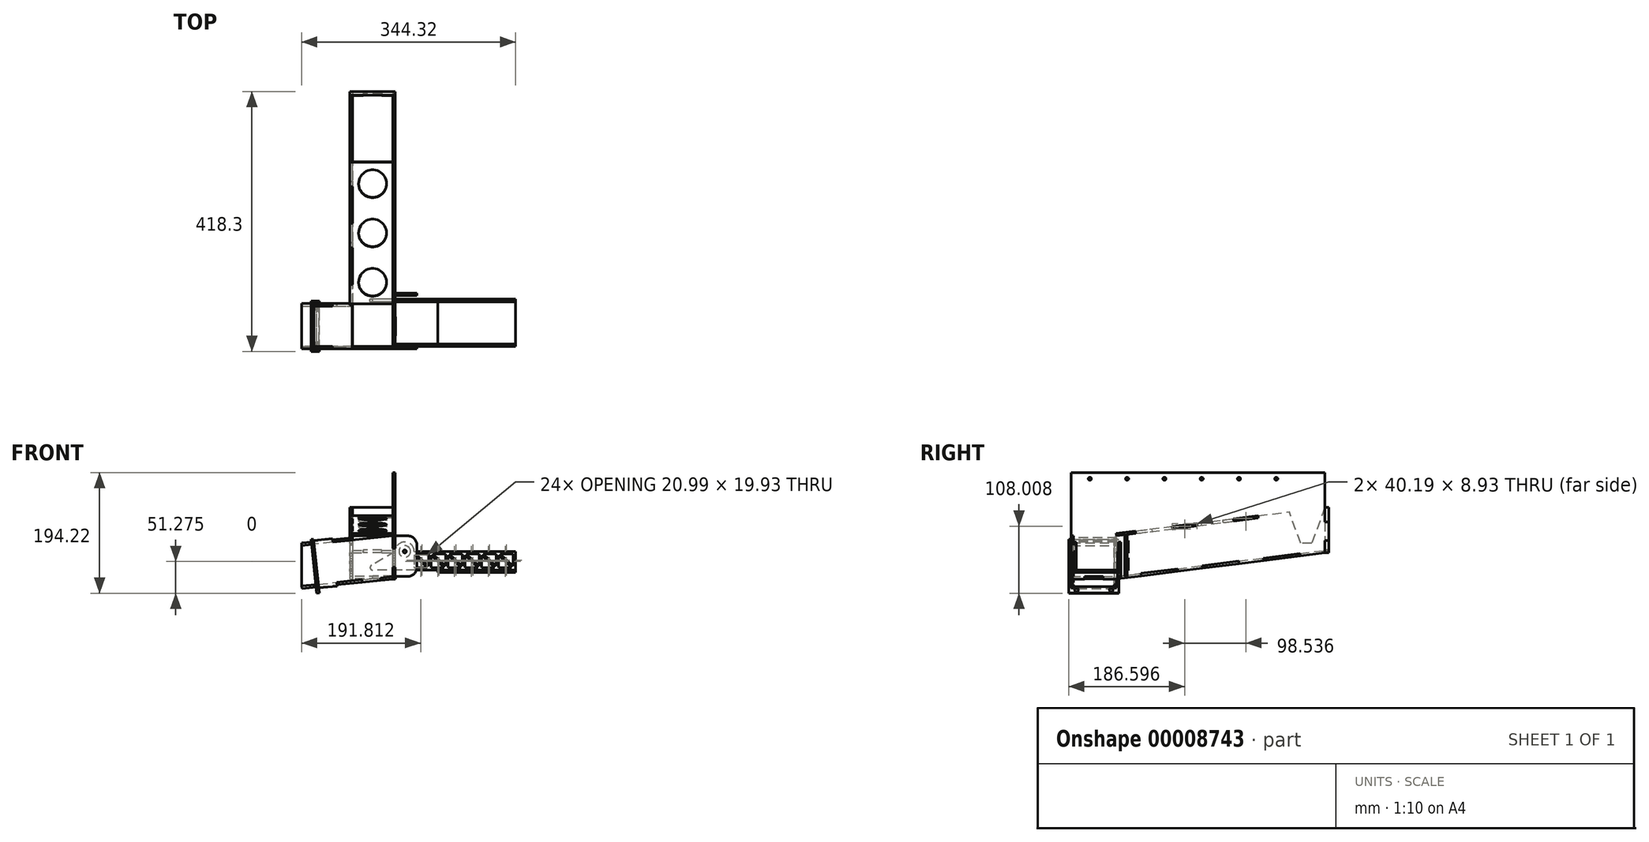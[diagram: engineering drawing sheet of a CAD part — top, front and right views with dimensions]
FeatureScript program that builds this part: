
annotation { "Feature Type Name" : "Feature", "Feature Type Description" : "" }
export const myFeature = defineFeature(function(context is Context, id is Id, definition is map)
    precondition{}
    {
        {
            var Q0;
            Q0=qCreatedBy(makeId("Front.planeOp"),FACE);
            var sketch = newSketch(context, id + "F0", { "sketchPlane" : qUnion([Q0])});
            skCircle(sketch, "E0", {"center": v(0, 0) * mm, "radius": 150 * mm, "construction": true});
            skLineSegment(sketch, "E1", {"start": v(0, 150) * mm, "end": v(0, -150) * mm, "construction": true});
            skSolve(sketch);
        }
        {
            var Q0;
            Q0=qCreatedBy(makeId("Front.planeOp"),FACE);
            var sketch = newSketch(context, id + "F1", { "sketchPlane" : qUnion([Q0])});
            skLineSegment(sketch, "E2", {"start": v(-146.4, 32.68) * mm, "end": v(-146.4, -32.68) * mm});
            skLineSegment(sketch, "E3", {"start": v(-146.4, -32.68) * mm, "end": v(-119.71, -29.87) * mm});
            skLineSegment(sketch, "E4", {"start": v(0, -17.3) * mm, "end": v(0, -2.3) * mm});
            skLineSegment(sketch, "E5", {"start": v(0, 48.07) * mm, "end": v(-96.67, 37.9) * mm});
            skLineSegment(sketch, "E6.bottom", {"start": v(0, -17.3) * mm, "end": v(-73, -17.3) * mm, "construction": true});
            skLineSegment(sketch, "E6.top", {"start": v(0, 48.07) * mm, "end": v(-73, 48.07) * mm, "construction": true});
            skLineSegment(sketch, "E6.left", {"start": v(0, -17.3) * mm, "end": v(0, 48.07) * mm, "construction": true});
            skLineSegment(sketch, "E6.right", {"start": v(-73, -17.3) * mm, "end": v(-73, 48.07) * mm, "construction": true});
            skLineSegment(sketch, "E7", {"start": v(-119.71, -29.87) * mm, "end": v(-119.09, -35.84) * mm});
            skLineSegment(sketch, "E8", {"start": v(-119.09, -35.84) * mm, "end": v(-89.25, -32.7) * mm});
            skLineSegment(sketch, "E9", {"start": v(-89.25, -32.7) * mm, "end": v(-89.88, -26.74) * mm});
            skLineSegment(sketch, "E10", {"start": v(-49.73, -22.52) * mm, "end": v(-49.3, -26.5) * mm});
            skLineSegment(sketch, "E11", {"start": v(-49.3, -26.5) * mm, "end": v(-19.47, -23.36) * mm});
            skLineSegment(sketch, "E12", {"start": v(-19.47, -23.36) * mm, "end": v(-19.9, -19.38) * mm});
            skLineSegment(sketch, "E13", {"start": v(-126.5, 34.77) * mm, "end": v(-127.13, 40.74) * mm});
            skLineSegment(sketch, "E14", {"start": v(-127.13, 40.74) * mm, "end": v(-97.3, 43.87) * mm});
            skLineSegment(sketch, "E15", {"start": v(-97.3, 43.87) * mm, "end": v(-96.67, 37.9) * mm});
            skLineSegment(sketch, "E16", {"start": v(0, 27.7) * mm, "end": v(4, 27.7) * mm});
            skLineSegment(sketch, "E17", {"start": v(4, -2.3) * mm, "end": v(0, -2.3) * mm});
            skLineSegment(sketch, "E18", {"start": v(-146.4, 32.68) * mm, "end": v(-139.6, -31.96) * mm, "construction": true});
            skLineSegment(sketch, "E19.trimOffspring", {"start": v(-89.88, -26.74) * mm, "end": v(-49.73, -22.52) * mm});
            skLineSegment(sketch, "E20.trimOffspring", {"start": v(-126.5, 34.77) * mm, "end": v(-146.4, 32.68) * mm});
            skLineSegment(sketch, "E21.trimOffspring", {"start": v(-19.9, -19.38) * mm, "end": v(0, -17.3) * mm});
            skLineSegment(sketch, "E22.trimOffspring", {"start": v(0, 27.7) * mm, "end": v(0, 48.07) * mm});
            skLineSegment(sketch, "E23.bottom", {"start": v(4, 48.07) * mm, "end": v(24, 48.07) * mm});
            skLineSegment(sketch, "E23.top", {"start": v(4, -17.3) * mm, "end": v(24, -17.3) * mm});
            skLineSegment(sketch, "E23.left", {"start": v(4, 48.07) * mm, "end": v(4, 27.7) * mm});
            skLineSegment(sketch, "E23.right", {"start": v(39, 33.07) * mm, "end": v(39, -2.3) * mm});
            skLineSegment(sketch, "E24.trimOffspring", {"start": v(4, -2.3) * mm, "end": v(4, -17.3) * mm});
            skCircle(sketch, "E25", {"center": v(19.25, 23.09) * mm, "radius": 2.5 * mm});
            skPoint(sketch, "E26.visualSharp", {"position": v(39, 48.07) * mm});
            skArc(sketch, "E26.filletArc", {"start": v(39, 33.07) * mm, "mid": v(34.6, 43.67) * mm, "end": v(24, 48.07) * mm});
            skPoint(sketch, "E27.visualSharp", {"position": v(39, -17.3) * mm});
            skArc(sketch, "E27.filletArc", {"start": v(24, -17.3) * mm, "mid": v(34.6, -12.9) * mm, "end": v(39, -2.3) * mm});
            skSolve(sketch);
        }
        {
            var Q0;
            Q0 = qSketchRegion(id + "F1", true);
            extrude(context, id + "F2", {"entities" : qUnion([Q0]), "depth" : 4 * mm});
        }
        {
            var Q0;
            Q0=makeQuery(id+"F2.opExtrude","SWEPT_FACE",FACE,{"disambiguationData":[OSD([sQuery(id+"F1.wireOp",EDGE,"E3")])]});
            var sketch = newSketch(context, id + "F3", { "sketchPlane" : qUnion([Q0])});
            skLineSegment(sketch, "E28.bottom", {"start": v(-149.01, 4) * mm, "end": v(-122.18, 4) * mm});
            skLineSegment(sketch, "E28.top", {"start": v(-149.01, -69) * mm, "end": v(-122.18, -69) * mm});
            skLineSegment(sketch, "E28.left", {"start": v(-149.01, 4) * mm, "end": v(-149.01, -69) * mm});
            skLineSegment(sketch, "E28.right", {"start": v(-1.8, 4) * mm, "end": v(-1.8, -17.5) * mm});
            skLineSegment(sketch, "E29", {"start": v(-122.18, 4) * mm, "end": v(-122.18, 0) * mm});
            skLineSegment(sketch, "E30", {"start": v(-122.18, 0) * mm, "end": v(-92.18, 0) * mm});
            skLineSegment(sketch, "E31", {"start": v(-92.18, 0) * mm, "end": v(-92.18, 4) * mm});
            skLineSegment(sketch, "E32.0.0", {"start": v(-51.8, 0) * mm, "end": v(-21.8, 0) * mm});
            skLineSegment(sketch, "E32.0.1", {"start": v(-21.8, 0) * mm, "end": v(-21.8, 4) * mm});
            skLineSegment(sketch, "E32.0.3", {"start": v(-51.8, 4) * mm, "end": v(-51.8, 0) * mm});
            skLineSegment(sketch, "E33.trimOffspring", {"start": v(-21.8, 4) * mm, "end": v(-1.8, 4) * mm});
            skLineSegment(sketch, "E34.trimOffspring", {"start": v(-92.18, 4) * mm, "end": v(-51.8, 4) * mm});
            skLineSegment(sketch, "E35", {"start": v(-1.8, -17.5) * mm, "end": v(2.2, -17.5) * mm});
            skLineSegment(sketch, "E36", {"start": v(2.2, -17.5) * mm, "end": v(2.2, -47.5) * mm});
            skLineSegment(sketch, "E37", {"start": v(2.2, -47.5) * mm, "end": v(-1.8, -47.5) * mm});
            skLineSegment(sketch, "E38.trimOffspring", {"start": v(-1.8, -47.5) * mm, "end": v(-1.8, -69) * mm});
            skLineSegment(sketch, "E39", {"start": v(-122.18, -69) * mm, "end": v(-122.18, -65) * mm});
            skLineSegment(sketch, "E40", {"start": v(-122.18, -65) * mm, "end": v(-92.18, -65) * mm});
            skLineSegment(sketch, "E41", {"start": v(-92.18, -65) * mm, "end": v(-92.18, -69) * mm});
            skLineSegment(sketch, "E42.trimOffspring", {"start": v(-92.18, -69) * mm, "end": v(-1.8, -69) * mm});
            skSolve(sketch);
        }
        {
            var Q0;
            Q0 = qSketchRegion(id + "F3", true);
            extrude(context, id + "F4", {"entities" : qUnion([Q0]), "depth" : 4 * mm});
        }
        {
            var Q0;
            Q0=makeQuery(id+"F2.opExtrude","SWEPT_FACE",FACE,{"disambiguationData":[OSD([sQuery(id+"F1.wireOp",EDGE,"E22.trimOffspring")])]});
            var sketch = newSketch(context, id + "F5", { "sketchPlane" : qUnion([Q0])});
            skLineSegment(sketch, "E43", {"start": v(404.3, 20.66) * mm, "end": v(404.3, 40.33) * mm});
            skLineSegment(sketch, "E44", {"start": v(404.3, 90) * mm, "end": v(356.07, 83.97) * mm});
            skLineSegment(sketch, "E45", {"start": v(69, 48.07) * mm, "end": v(-4, 48.07) * mm, "construction": true});
            skLineSegment(sketch, "E46", {"start": v(-4, 48.07) * mm, "end": v(-4, 27.7) * mm});
            skLineSegment(sketch, "E47", {"start": v(-4, 27.7) * mm, "end": v(0, 27.7) * mm});
            skLineSegment(sketch, "E48", {"start": v(0, 27.7) * mm, "end": v(0, -2.3) * mm});
            skLineSegment(sketch, "E49", {"start": v(0, -2.3) * mm, "end": v(-4, -2.3) * mm});
            skLineSegment(sketch, "E50", {"start": v(-4, -2.3) * mm, "end": v(-4, -21.27) * mm});
            skLineSegment(sketch, "E51", {"start": v(-4, -21.27) * mm, "end": v(17.5, -21.27) * mm});
            skLineSegment(sketch, "E52", {"start": v(17.5, -21.27) * mm, "end": v(17.5, -16.87) * mm});
            skLineSegment(sketch, "E53", {"start": v(17.5, -16.87) * mm, "end": v(47.5, -16.87) * mm});
            skLineSegment(sketch, "E54", {"start": v(47.5, -16.87) * mm, "end": v(47.5, -21.27) * mm});
            skLineSegment(sketch, "E55", {"start": v(47.5, -21.27) * mm, "end": v(69, -21.27) * mm});
            skLineSegment(sketch, "E56", {"start": v(32.5, 48.07) * mm, "end": v(32.5, -16.87) * mm, "construction": true});
            skCircle(sketch, "E57", {"center": v(32.5, 0) * mm, "radius": 150 * mm, "construction": true});
            skLineSegment(sketch, "E58", {"start": v(-117.5, 0) * mm, "end": v(-117.5, -150) * mm, "construction": true});
            skLineSegment(sketch, "E59", {"start": v(-117.5, -150) * mm, "end": v(404.3, -150) * mm, "construction": true});
            skLineSegment(sketch, "E60", {"start": v(404.3, -150) * mm, "end": v(404.3, 150) * mm, "construction": true});
            skLineSegment(sketch, "E61", {"start": v(404.3, 150) * mm, "end": v(-117.5, 150) * mm, "construction": true});
            skLineSegment(sketch, "E62", {"start": v(-117.5, 0) * mm, "end": v(-117.5, 150) * mm, "construction": true});
            skLineSegment(sketch, "E63", {"start": v(404.3, 70.33) * mm, "end": v(410.3, 70.33) * mm});
            skLineSegment(sketch, "E64", {"start": v(410.3, 70.33) * mm, "end": v(410.3, 40.33) * mm});
            skLineSegment(sketch, "E65", {"start": v(410.3, 40.33) * mm, "end": v(404.3, 40.33) * mm});
            skLineSegment(sketch, "E66.trimOffspring", {"start": v(404.3, 70.33) * mm, "end": v(404.3, 90) * mm});
            skLineSegment(sketch, "E67", {"start": v(108.7, -16.3) * mm, "end": v(108.2, -12.34) * mm});
            skLineSegment(sketch, "E68", {"start": v(108.2, -12.34) * mm, "end": v(167.04, -4.98) * mm});
            skLineSegment(sketch, "E69", {"start": v(167.04, -4.98) * mm, "end": v(167.54, -8.95) * mm});
            skLineSegment(sketch, "E70", {"start": v(207.23, -3.98) * mm, "end": v(206.73, -0.01) * mm});
            skLineSegment(sketch, "E71", {"start": v(206.73, -0.01) * mm, "end": v(265.58, 7.35) * mm});
            skLineSegment(sketch, "E72", {"start": v(265.58, 7.35) * mm, "end": v(266.07, 3.38) * mm});
            skLineSegment(sketch, "E73", {"start": v(305.76, 8.34) * mm, "end": v(305.27, 12.3) * mm});
            skLineSegment(sketch, "E74", {"start": v(305.27, 12.3) * mm, "end": v(364.11, 19.67) * mm});
            skLineSegment(sketch, "E75", {"start": v(364.11, 19.67) * mm, "end": v(364.6, 15.7) * mm});
            skLineSegment(sketch, "E76.trimOffspring", {"start": v(167.54, -8.95) * mm, "end": v(207.23, -3.98) * mm});
            skLineSegment(sketch, "E77.trimOffspring", {"start": v(364.6, 15.7) * mm, "end": v(404.3, 20.66) * mm});
            skLineSegment(sketch, "E78", {"start": v(108.7, -16.3) * mm, "end": v(76, -20.4) * mm});
            skLineSegment(sketch, "E79.trimOffspring", {"start": v(266.07, 3.38) * mm, "end": v(305.76, 8.34) * mm});
            skLineSegment(sketch, "E80", {"start": v(100.15, 51.96) * mm, "end": v(99.66, 55.93) * mm});
            skLineSegment(sketch, "E81", {"start": v(99.66, 55.93) * mm, "end": v(158.5, 63.3) * mm, "construction": true});
            skLineSegment(sketch, "E82", {"start": v(158.5, 63.3) * mm, "end": v(159, 59.32) * mm});
            skLineSegment(sketch, "E83", {"start": v(198.69, 64.29) * mm, "end": v(198.2, 68.25) * mm});
            skLineSegment(sketch, "E84", {"start": v(198.2, 68.25) * mm, "end": v(257.04, 75.61) * mm, "construction": true});
            skLineSegment(sketch, "E85", {"start": v(257.04, 75.61) * mm, "end": v(257.53, 71.64) * mm});
            skLineSegment(sketch, "E86", {"start": v(297.23, 76.6) * mm, "end": v(296.73, 80.58) * mm});
            skLineSegment(sketch, "E87", {"start": v(296.73, 80.58) * mm, "end": v(355.57, 87.94) * mm, "construction": true});
            skLineSegment(sketch, "E88", {"start": v(355.57, 87.94) * mm, "end": v(356.07, 83.97) * mm});
            skLineSegment(sketch, "E89.trimOffspring", {"start": v(100.15, 51.96) * mm, "end": v(69, 48.07) * mm});
            skLineSegment(sketch, "E90.trimOffspring", {"start": v(198.69, 64.29) * mm, "end": v(159, 59.32) * mm});
            skLineSegment(sketch, "E91.trimOffspring", {"start": v(297.23, 76.6) * mm, "end": v(257.53, 71.64) * mm});
            skLineSegment(sketch, "E92.bottom", {"start": v(71, 23.09) * mm, "end": v(76, 23.09) * mm});
            skLineSegment(sketch, "E92.top", {"start": v(71, -6.91) * mm, "end": v(76, -6.91) * mm, "construction": true});
            skLineSegment(sketch, "E92.left", {"start": v(71, 23.09) * mm, "end": v(71, -6.91) * mm});
            skLineSegment(sketch, "E92.right", {"start": v(76, 23.09) * mm, "end": v(76, -6.91) * mm});
            skLineSegment(sketch, "E93", {"start": v(76, -6.91) * mm, "end": v(76, -20.4) * mm});
            skLineSegment(sketch, "E94", {"start": v(71, -6.91) * mm, "end": v(71, -21.02) * mm});
            skLineSegment(sketch, "E95.trimOffspring", {"start": v(71, -21.02) * mm, "end": v(69, -21.27) * mm});
            skLineSegment(sketch, "E96", {"start": v(404.3, 90) * mm, "end": v(404.3, 150) * mm});
            skLineSegment(sketch, "E97", {"start": v(404.3, 150) * mm, "end": v(-4, 150) * mm});
            skLineSegment(sketch, "E98", {"start": v(-4, 48.07) * mm, "end": v(-4, 150) * mm});
            skLineSegment(sketch, "E99", {"start": v(158.5, 63.3) * mm, "end": v(198.2, 68.25) * mm});
            skLineSegment(sketch, "E100", {"start": v(257.04, 75.61) * mm, "end": v(296.73, 80.58) * mm});
            skLineSegment(sketch, "E101", {"start": v(355.57, 87.94) * mm, "end": v(404.3, 94.03) * mm});
            skLineSegment(sketch, "E102", {"start": v(69, 48.07) * mm, "end": v(68.5, 52.04) * mm});
            skLineSegment(sketch, "E103", {"start": v(68.5, 52.04) * mm, "end": v(99.66, 55.93) * mm});
            skCircle(sketch, "E104", {"center": v(26, 140) * mm, "radius": 2.5 * mm});
            skCircle(sketch, "E105", {"center": v(86, 140) * mm, "radius": 2.5 * mm});
            skCircle(sketch, "E106", {"center": v(146, 140) * mm, "radius": 2.5 * mm});
            skCircle(sketch, "E107", {"center": v(206, 140) * mm, "radius": 2.5 * mm});
            skCircle(sketch, "E108", {"center": v(266, 140) * mm, "radius": 2.5 * mm});
            skCircle(sketch, "E109", {"center": v(326, 140) * mm, "radius": 2.5 * mm});
            skCircle(sketch, "E110", {"center": v(374.3, 120) * mm, "radius": 30 * mm, "construction": true});
            skLineSegment(sketch, "E111.bottom", {"start": v(82, 40.6) * mm, "end": v(88, 40.6) * mm});
            skLineSegment(sketch, "E111.top", {"start": v(82, 20.6) * mm, "end": v(88, 20.6) * mm});
            skLineSegment(sketch, "E111.left", {"start": v(82, 40.6) * mm, "end": v(82, 20.6) * mm});
            skLineSegment(sketch, "E111.right", {"start": v(88, 40.6) * mm, "end": v(88, 20.6) * mm});
            skLineSegment(sketch, "E112.bottom", {"start": v(82, 12.6) * mm, "end": v(88, 12.6) * mm});
            skLineSegment(sketch, "E112.top", {"start": v(82, -7.4) * mm, "end": v(88, -7.4) * mm});
            skLineSegment(sketch, "E112.left", {"start": v(82, 12.6) * mm, "end": v(82, -7.4) * mm});
            skLineSegment(sketch, "E112.right", {"start": v(88, 12.6) * mm, "end": v(88, -7.4) * mm});
            skSolve(sketch);
        }
        {
            var Q0;
            Q0 = qSketchRegion(id + "F5", true);
            extrude(context, id + "F6", {"entities" : qUnion([Q0]), "depth" : 4 * mm});
        }
        {
            var Q0;
            Q0=makeQuery(id+"F6.opExtrude","SWEPT_FACE",FACE,{"disambiguationData":[OSD([sQuery(id+"F5.wireOp",EDGE,"E71")])]});
            var sketch = newSketch(context, id + "F7", { "sketchPlane" : qUnion([Q0])});
            skLineSegment(sketch, "E113", {"start": v(-65, -66.32) * mm, "end": v(-65, -105.83) * mm});
            skLineSegment(sketch, "E114", {"start": v(-65, -403.74) * mm, "end": v(-47.5, -403.74) * mm});
            skLineSegment(sketch, "E115", {"start": v(4, -363.74) * mm, "end": v(4, -304.44) * mm});
            skLineSegment(sketch, "E116.0.0", {"start": v(0, -363.74) * mm, "end": v(0, -403.74) * mm});
            skLineSegment(sketch, "E116.0.3", {"start": v(4, -363.74) * mm, "end": v(0, -363.74) * mm});
            skPoint(sketch, "E116.0.1.end.orphan", {"position": v(4, -403.74) * mm});
            skLineSegment(sketch, "E117.0.0", {"start": v(0, -264.44) * mm, "end": v(0, -304.44) * mm});
            skLineSegment(sketch, "E117.0.1", {"start": v(0, -304.44) * mm, "end": v(4, -304.44) * mm});
            skLineSegment(sketch, "E117.0.3", {"start": v(4, -264.44) * mm, "end": v(0, -264.44) * mm});
            skLineSegment(sketch, "E118.trimOffspring", {"start": v(4, -264.44) * mm, "end": v(4, -205.13) * mm});
            skLineSegment(sketch, "E119.0.0", {"start": v(0, -165.13) * mm, "end": v(0, -205.13) * mm});
            skLineSegment(sketch, "E119.0.1", {"start": v(0, -205.13) * mm, "end": v(4, -205.13) * mm});
            skLineSegment(sketch, "E119.0.3", {"start": v(4, -165.13) * mm, "end": v(0, -165.13) * mm});
            skLineSegment(sketch, "E120.trimOffspring", {"start": v(4, -165.13) * mm, "end": v(4, -105.83) * mm});
            skLineSegment(sketch, "E121.0.0", {"start": v(0, -66.32) * mm, "end": v(0, -67.38) * mm});
            skLineSegment(sketch, "E121.0.1", {"start": v(0, -105.83) * mm, "end": v(4, -105.83) * mm});
            skLineSegment(sketch, "E122", {"start": v(0, -66.32) * mm, "end": v(-65, -66.32) * mm});
            skLineSegment(sketch, "E123", {"start": v(-32.5, -403.74) * mm, "end": v(-32.5, -66.32) * mm, "construction": true});
            skLineSegment(sketch, "E124.0.MirrorCS", {"start": v(-65, -105.83) * mm, "end": v(-69, -105.83) * mm});
            skLineSegment(sketch, "E125.0.MirrorCS", {"start": v(-69, -165.13) * mm, "end": v(-69, -105.83) * mm});
            skLineSegment(sketch, "E126.0.MirrorCS", {"start": v(-69, -165.13) * mm, "end": v(-65, -165.13) * mm});
            skLineSegment(sketch, "E127.0.MirrorCS", {"start": v(-65, -205.13) * mm, "end": v(-69, -205.13) * mm});
            skLineSegment(sketch, "E128.0.MirrorCS", {"start": v(-69, -264.44) * mm, "end": v(-69, -205.13) * mm});
            skLineSegment(sketch, "E129.0.MirrorCS", {"start": v(-69, -264.44) * mm, "end": v(-65, -264.44) * mm});
            skLineSegment(sketch, "E130.0.MirrorCS", {"start": v(-65, -304.44) * mm, "end": v(-69, -304.44) * mm});
            skLineSegment(sketch, "E131.0.MirrorCS", {"start": v(-69, -363.74) * mm, "end": v(-69, -304.44) * mm});
            skLineSegment(sketch, "E132.0.MirrorCS", {"start": v(-69, -363.74) * mm, "end": v(-65, -363.74) * mm});
            skLineSegment(sketch, "E133.trimOffspring", {"start": v(-65, -165.13) * mm, "end": v(-65, -205.13) * mm});
            skLineSegment(sketch, "E134.trimOffspring", {"start": v(-65, -264.44) * mm, "end": v(-65, -304.44) * mm});
            skLineSegment(sketch, "E135.trimOffspring", {"start": v(-65, -363.74) * mm, "end": v(-65, -403.74) * mm});
            skLineSegment(sketch, "E136", {"start": v(-17.5, -403.74) * mm, "end": v(-17.5, -407.74) * mm});
            skLineSegment(sketch, "E137", {"start": v(-17.5, -407.74) * mm, "end": v(-47.5, -407.74) * mm});
            skLineSegment(sketch, "E138", {"start": v(-47.5, -407.74) * mm, "end": v(-47.5, -403.74) * mm});
            skLineSegment(sketch, "E139.trimOffspring", {"start": v(-17.5, -403.74) * mm, "end": v(0, -403.74) * mm});
            skLineSegment(sketch, "E140.bottom", {"start": v(0, -67.38) * mm, "end": v(-32.5, -67.38) * mm});
            skLineSegment(sketch, "E140.top", {"start": v(0, -73.38) * mm, "end": v(-32.5, -73.38) * mm});
            skLineSegment(sketch, "E140.right", {"start": v(-32.5, -67.38) * mm, "end": v(-32.5, -73.38) * mm});
            skLineSegment(sketch, "E141.trimOffspring", {"start": v(0, -73.38) * mm, "end": v(0, -105.83) * mm});
            skSolve(sketch);
        }
        {
            var Q0;
            Q0 = qSketchRegion(id + "F7", true);
            extrude(context, id + "F8", {"entities" : qUnion([Q0]), "depth" : 4 * mm});
        }
        {
            var Q0;
            Q0=makeQuery(id+"F8.opExtrude","SWEPT_FACE",FACE,{"disambiguationData":[OSD([sQuery(id+"F7.wireOp",EDGE,"E135.trimOffspring")])]});
            var sketch = newSketch(context, id + "F9", { "sketchPlane" : qUnion([Q0])});
            skLineSegment(sketch, "E142.0.0", {"start": v(-404.3, 20.66) * mm, "end": v(-364.6, 15.7) * mm});
            skLineSegment(sketch, "E142.0.1", {"start": v(-364.6, 15.7) * mm, "end": v(-364.11, 19.67) * mm});
            skLineSegment(sketch, "E142.0.2", {"start": v(-364.11, 19.67) * mm, "end": v(-305.27, 12.3) * mm});
            skLineSegment(sketch, "E142.0.3", {"start": v(-305.27, 12.3) * mm, "end": v(-305.76, 8.34) * mm});
            skLineSegment(sketch, "E142.0.4", {"start": v(-305.76, 8.34) * mm, "end": v(-266.07, 3.38) * mm});
            skLineSegment(sketch, "E142.0.5", {"start": v(-266.07, 3.38) * mm, "end": v(-265.58, 7.35) * mm});
            skLineSegment(sketch, "E142.0.6", {"start": v(-265.58, 7.35) * mm, "end": v(-206.73, -0.01) * mm});
            skLineSegment(sketch, "E142.0.7", {"start": v(-206.73, -0.01) * mm, "end": v(-207.23, -3.98) * mm});
            skLineSegment(sketch, "E142.0.8", {"start": v(-207.23, -3.98) * mm, "end": v(-167.54, -8.95) * mm});
            skLineSegment(sketch, "E142.0.9", {"start": v(-167.54, -8.95) * mm, "end": v(-167.04, -4.98) * mm});
            skLineSegment(sketch, "E142.0.10", {"start": v(-167.04, -4.98) * mm, "end": v(-108.2, -12.34) * mm});
            skLineSegment(sketch, "E142.0.11", {"start": v(-108.2, -12.34) * mm, "end": v(-108.7, -16.3) * mm});
            skLineSegment(sketch, "E142.0.12", {"start": v(-108.7, -16.3) * mm, "end": v(-69, -21.27) * mm});
            skLineSegment(sketch, "E142.0.24", {"start": v(-69, 48.07) * mm, "end": v(-100.15, 51.96) * mm});
            skLineSegment(sketch, "E142.0.25", {"start": v(-99.66, 55.93) * mm, "end": v(-100.15, 51.96) * mm});
            skLineSegment(sketch, "E142.0.26", {"start": v(-99.66, 55.93) * mm, "end": v(-158.5, 63.3) * mm});
            skLineSegment(sketch, "E142.0.27", {"start": v(-158.5, 63.3) * mm, "end": v(-159, 59.32) * mm});
            skLineSegment(sketch, "E142.0.28", {"start": v(-159, 59.32) * mm, "end": v(-198.69, 64.29) * mm});
            skLineSegment(sketch, "E142.0.29", {"start": v(-198.2, 68.25) * mm, "end": v(-198.69, 64.29) * mm});
            skLineSegment(sketch, "E142.0.30", {"start": v(-198.2, 68.25) * mm, "end": v(-257.04, 75.61) * mm});
            skLineSegment(sketch, "E142.0.31", {"start": v(-257.04, 75.61) * mm, "end": v(-257.53, 71.64) * mm});
            skLineSegment(sketch, "E142.0.32", {"start": v(-257.53, 71.64) * mm, "end": v(-297.23, 76.6) * mm});
            skLineSegment(sketch, "E142.0.33", {"start": v(-296.73, 80.58) * mm, "end": v(-297.23, 76.6) * mm});
            skLineSegment(sketch, "E142.0.34", {"start": v(-296.73, 80.58) * mm, "end": v(-346.91, 86.85) * mm});
            skLineSegment(sketch, "E142.0.37", {"start": v(-404.3, 94.03) * mm, "end": v(-404.3, 70.33) * mm});
            skLineSegment(sketch, "E142.0.38", {"start": v(-404.3, 70.33) * mm, "end": v(-410.3, 70.33) * mm});
            skLineSegment(sketch, "E142.0.39", {"start": v(-410.3, 70.33) * mm, "end": v(-410.3, 40.33) * mm});
            skLineSegment(sketch, "E142.0.40", {"start": v(-410.3, 40.33) * mm, "end": v(-404.3, 40.33) * mm});
            skLineSegment(sketch, "E142.0.41", {"start": v(-404.3, 40.33) * mm, "end": v(-404.3, 20.66) * mm});
            skLineSegment(sketch, "E143", {"start": v(-69, 45.23) * mm, "end": v(-69, 32.95) * mm});
            skLineSegment(sketch, "E144", {"start": v(-69, 32.95) * mm, "end": v(-65, 32.95) * mm});
            skLineSegment(sketch, "E145", {"start": v(-65, 32.95) * mm, "end": v(-65, 20.95) * mm});
            skLineSegment(sketch, "E146", {"start": v(-65, 20.95) * mm, "end": v(-69, 20.95) * mm});
            skLineSegment(sketch, "E147", {"start": v(-69, 5.84) * mm, "end": v(-65, 5.84) * mm});
            skLineSegment(sketch, "E148", {"start": v(-65, 5.84) * mm, "end": v(-65, -6.16) * mm});
            skLineSegment(sketch, "E149", {"start": v(-65, -6.16) * mm, "end": v(-69, -6.16) * mm});
            skLineSegment(sketch, "E150.trimOffspring", {"start": v(-69, 20.95) * mm, "end": v(-69, 5.84) * mm});
            skLineSegment(sketch, "E151.trimOffspring", {"start": v(-69, -6.16) * mm, "end": v(-69, -21.27) * mm});
            skCircle(sketch, "E152", {"center": v(-374.3, 51.18) * mm, "radius": 30 * mm, "construction": true});
            skLineSegment(sketch, "E153", {"start": v(-404.3, 94.03) * mm, "end": v(-383.24, 36.18) * mm});
            skLineSegment(sketch, "E154", {"start": v(-383.24, 36.18) * mm, "end": v(-365.36, 36.18) * mm});
            skLineSegment(sketch, "E155", {"start": v(-365.36, 36.18) * mm, "end": v(-346.91, 86.85) * mm});
            skLineSegment(sketch, "E156", {"start": v(-374.3, 36.18) * mm, "end": v(-374.3, 81.18) * mm, "construction": true});
            skPoint(sketch, "E142.0.35.end.orphan", {"position": v(-356.78, 84.6) * mm});
            skPoint(sketch, "E142.0.35.start.orphan", {"position": v(-355.27, 87.9) * mm});
            skLineSegment(sketch, "E157", {"start": v(-69, 48.07) * mm, "end": v(-67, 48.07) * mm});
            skLineSegment(sketch, "E158", {"start": v(-67, 48.07) * mm, "end": v(-67, 45.23) * mm});
            skLineSegment(sketch, "E159", {"start": v(-67, 45.23) * mm, "end": v(-69, 45.23) * mm});
            skLineSegment(sketch, "E160", {"start": v(-69, 32.95) * mm, "end": v(-69, 48.07) * mm, "construction": true});
            skSolve(sketch);
        }
        {
            var Q0;
            Q0 = qSketchRegion(id + "F9", true);
            extrude(context, id + "F10", {"entities" : qUnion([Q0]), "depth" : 4 * mm});
        }
        {
            var Q0;
            Q0=makeQuery(id+"F4.opExtrude","SWEPT_FACE",FACE,{"disambiguationData":[OSD([sQuery(id+"F3.wireOp",EDGE,"E28.top")])]});
            var sketch = newSketch(context, id + "F11", { "sketchPlane" : qUnion([Q0])});
            skLineSegment(sketch, "E161", {"start": v(146.4, -32.68) * mm, "end": v(146.4, 32.68) * mm});
            skLineSegment(sketch, "E162", {"start": v(146.4, 32.68) * mm, "end": v(126.5, 34.77) * mm});
            skLineSegment(sketch, "E163", {"start": v(126.5, 34.77) * mm, "end": v(127.13, 40.74) * mm});
            skLineSegment(sketch, "E164", {"start": v(127.13, 40.74) * mm, "end": v(97.3, 43.87) * mm});
            skLineSegment(sketch, "E165", {"start": v(96.67, 37.9) * mm, "end": v(97.3, 43.87) * mm});
            skLineSegment(sketch, "E166", {"start": v(96.67, 37.9) * mm, "end": v(65, 41.23) * mm});
            skLineSegment(sketch, "E167", {"start": v(65, 41.23) * mm, "end": v(65, 32.95) * mm});
            skLineSegment(sketch, "E168", {"start": v(65, 32.95) * mm, "end": v(69, 32.95) * mm});
            skLineSegment(sketch, "E169", {"start": v(69, 32.95) * mm, "end": v(69, 20.95) * mm});
            skLineSegment(sketch, "E170", {"start": v(69, 20.95) * mm, "end": v(65, 20.95) * mm});
            skLineSegment(sketch, "E171", {"start": v(65, 20.95) * mm, "end": v(65, 5.84) * mm});
            skLineSegment(sketch, "E172", {"start": v(65, 5.84) * mm, "end": v(69, 5.84) * mm});
            skLineSegment(sketch, "E173", {"start": v(69, 5.84) * mm, "end": v(69, -6.16) * mm});
            skLineSegment(sketch, "E174", {"start": v(69, -6.16) * mm, "end": v(65, -6.16) * mm});
            skLineSegment(sketch, "E175", {"start": v(65, -6.16) * mm, "end": v(65, -24.12) * mm});
            skLineSegment(sketch, "E176", {"start": v(146.4, -32.68) * mm, "end": v(119.71, -29.87) * mm});
            skLineSegment(sketch, "E177", {"start": v(89.25, -32.7) * mm, "end": v(89.88, -26.74) * mm});
            skLineSegment(sketch, "E178", {"start": v(89.88, -26.74) * mm, "end": v(65, -24.12) * mm});
            skLineSegment(sketch, "E179", {"start": v(119.71, -29.87) * mm, "end": v(119.09, -35.84) * mm});
            skLineSegment(sketch, "E180", {"start": v(119.09, -35.84) * mm, "end": v(89.25, -32.7) * mm});
            skSolve(sketch);
        }
        {
            var Q0;
            Q0 = qSketchRegion(id + "F11", true);
            extrude(context, id + "F12", {"entities" : qUnion([Q0]), "oppositeDirection" : true, "depth" : 4 * mm});
        }
        {
            var Q0;
            Q0=makeQuery(id+"F12.opExtrude","SWEPT_FACE",FACE,{"disambiguationData":[OSD([sQuery(id+"F11.wireOp",EDGE,"E162")])]});
            var sketch = newSketch(context, id + "F13", { "sketchPlane" : qUnion([Q0])});
            skLineSegment(sketch, "E181.bottom", {"start": v(-142.18, 69) * mm, "end": v(-122.18, 69) * mm});
            skLineSegment(sketch, "E181.top", {"start": v(-142.18, -4) * mm, "end": v(-122.18, -4) * mm});
            skLineSegment(sketch, "E181.left", {"start": v(-142.18, 69) * mm, "end": v(-142.18, -4) * mm});
            skLineSegment(sketch, "E181.right", {"start": v(-60.33, 69) * mm, "end": v(-60.33, -4) * mm});
            skLineSegment(sketch, "E182.0.1", {"start": v(-122.18, 69) * mm, "end": v(-122.18, 65) * mm});
            skLineSegment(sketch, "E182.0.2", {"start": v(-122.18, 65) * mm, "end": v(-92.18, 65) * mm});
            skLineSegment(sketch, "E182.0.3", {"start": v(-92.18, 65) * mm, "end": v(-92.18, 69) * mm});
            skLineSegment(sketch, "E183.0.0", {"start": v(-92.18, 0) * mm, "end": v(-122.18, 0) * mm});
            skLineSegment(sketch, "E183.0.1", {"start": v(-122.18, 0) * mm, "end": v(-122.18, -4) * mm});
            skLineSegment(sketch, "E183.0.3", {"start": v(-92.18, -4) * mm, "end": v(-92.18, 0) * mm});
            skLineSegment(sketch, "E184.trimOffspring", {"start": v(-92.18, 69) * mm, "end": v(-60.33, 69) * mm});
            skLineSegment(sketch, "E185.trimOffspring", {"start": v(-92.18, -4) * mm, "end": v(-60.33, -4) * mm});
            skSolve(sketch);
        }
        {
            var Q0;
            Q0 = qSketchRegion(id + "F13", true);
            extrude(context, id + "F14", {"entities" : qUnion([Q0]), "depth" : 4 * mm});
        }
        {
            var Q0;
            Q0=makeQuery(id+"F10.opExtrude","SWEPT_FACE",FACE,{"disambiguationData":[OSD([sQuery(id+"F9.wireOp",EDGE,"E142.0.41")])]});
            var sketch = newSketch(context, id + "F15", { "sketchPlane" : qUnion([Q0])});
            skLineSegment(sketch, "E186.bottom", {"start": v(69, 20.66) * mm, "end": v(47.5, 20.66) * mm});
            skLineSegment(sketch, "E186.left", {"start": v(69, 20.66) * mm, "end": v(69, 40.33) * mm});
            skLineSegment(sketch, "E186.right", {"start": v(-4, 20.66) * mm, "end": v(-4, 40.33) * mm});
            skLineSegment(sketch, "E187.0.0", {"start": v(0, 40.33) * mm, "end": v(0, 70.33) * mm});
            skLineSegment(sketch, "E187.0.3", {"start": v(-4, 40.33) * mm, "end": v(0, 40.33) * mm});
            skLineSegment(sketch, "E188.0.0", {"start": v(65, 70.33) * mm, "end": v(65, 40.33) * mm});
            skLineSegment(sketch, "E188.0.1", {"start": v(65, 40.33) * mm, "end": v(69, 40.33) * mm});
            skLineSegment(sketch, "E189", {"start": v(17.5, 20.66) * mm, "end": v(17.5, 25.13) * mm});
            skLineSegment(sketch, "E190", {"start": v(17.5, 25.13) * mm, "end": v(47.5, 25.13) * mm});
            skLineSegment(sketch, "E191", {"start": v(47.5, 25.13) * mm, "end": v(47.5, 20.66) * mm});
            skLineSegment(sketch, "E192.trimOffspring", {"start": v(17.5, 20.66) * mm, "end": v(-4, 20.66) * mm});
            skLineSegment(sketch, "E193", {"start": v(0, 70.33) * mm, "end": v(-4, 70.33) * mm});
            skLineSegment(sketch, "E194", {"start": v(-4, 70.33) * mm, "end": v(-4, 94.03) * mm});
            skLineSegment(sketch, "E195", {"start": v(-4, 94.03) * mm, "end": v(69, 94.03) * mm});
            skLineSegment(sketch, "E196", {"start": v(69, 94.03) * mm, "end": v(69, 70.33) * mm});
            skLineSegment(sketch, "E197", {"start": v(69, 70.33) * mm, "end": v(65, 70.33) * mm});
            skSolve(sketch);
        }
        {
            var Q0;
            Q0 = qSketchRegion(id + "F15", true);
            extrude(context, id + "F16", {"entities" : qUnion([Q0]), "depth" : 6 * mm});
        }
        {
            var Q0;
            Q0=makeQuery(id+"F6.opExtrude","SWEPT_FACE",FACE,{"disambiguationData":[OSD([sQuery(id+"F5.wireOp",EDGE,"E91.trimOffspring")])]});
            var sketch = newSketch(context, id + "F17", { "sketchPlane" : qUnion([Q0])});
            skLineSegment(sketch, "E198.bottom", {"start": v(4, 304.44) * mm, "end": v(-69, 304.44) * mm});
            skLineSegment(sketch, "E198.top", {"start": v(4, 74.43) * mm, "end": v(-69, 74.43) * mm});
            skLineSegment(sketch, "E198.left", {"start": v(4, 304.44) * mm, "end": v(4, 264.44) * mm});
            skLineSegment(sketch, "E198.right", {"start": v(-69, 304.44) * mm, "end": v(-69, 264.44) * mm});
            skLineSegment(sketch, "E199.0.0", {"start": v(0, 165.13) * mm, "end": v(0, 105.83) * mm});
            skLineSegment(sketch, "E199.0.1", {"start": v(0, 105.83) * mm, "end": v(4, 105.83) * mm});
            skLineSegment(sketch, "E199.0.3", {"start": v(4, 165.13) * mm, "end": v(0, 165.13) * mm});
            skLineSegment(sketch, "E199.1.0", {"start": v(0, 264.44) * mm, "end": v(0, 205.13) * mm});
            skLineSegment(sketch, "E199.1.1", {"start": v(0, 205.13) * mm, "end": v(4, 205.13) * mm});
            skLineSegment(sketch, "E199.1.3", {"start": v(4, 264.44) * mm, "end": v(0, 264.44) * mm});
            skLineSegment(sketch, "E199.2.0", {"start": v(-65, 205.13) * mm, "end": v(-65, 264.44) * mm});
            skLineSegment(sketch, "E199.2.1", {"start": v(-65, 264.44) * mm, "end": v(-69, 264.44) * mm});
            skLineSegment(sketch, "E199.2.3", {"start": v(-69, 205.13) * mm, "end": v(-65, 205.13) * mm});
            skLineSegment(sketch, "E199.3.0", {"start": v(-65, 105.83) * mm, "end": v(-65, 165.13) * mm});
            skLineSegment(sketch, "E199.3.1", {"start": v(-65, 165.13) * mm, "end": v(-69, 165.13) * mm});
            skLineSegment(sketch, "E199.3.3", {"start": v(-69, 105.83) * mm, "end": v(-65, 105.83) * mm});
            skLineSegment(sketch, "E200.trimOffspring", {"start": v(4, 205.13) * mm, "end": v(4, 165.13) * mm});
            skLineSegment(sketch, "E201.trimOffspring", {"start": v(4, 105.83) * mm, "end": v(4, 74.43) * mm});
            skLineSegment(sketch, "E202.trimOffspring", {"start": v(-69, 205.13) * mm, "end": v(-69, 165.13) * mm});
            skLineSegment(sketch, "E203.trimOffspring", {"start": v(-69, 105.83) * mm, "end": v(-69, 74.43) * mm});
            skLineSegment(sketch, "E204", {"start": v(-32.5, 304.44) * mm, "end": v(-32.5, 74.43) * mm, "construction": true});
            skCircle(sketch, "E205", {"center": v(-32.5, 269.43) * mm, "radius": 22.5 * mm});
            skCircle(sketch, "E206", {"center": v(-32.5, 189.43) * mm, "radius": 22.5 * mm});
            skCircle(sketch, "E207", {"center": v(-32.5, 109.43) * mm, "radius": 22.5 * mm});
            skSolve(sketch);
        }
        {
            var Q0;
            Q0 = qSketchRegion(id + "F17", true);
            extrude(context, id + "F18", {"entities" : qUnion([Q0]), "depth" : 4 * mm});
        }
        {
            var Q0;
            Q0=makeQuery(id+"F2.opExtrude","SWEPT_FACE",FACE,{"disambiguationData":[OSD([sQuery(id+"F1.wireOp",EDGE,"E13")])]});
            var sketch = newSketch(context, id + "F19", { "sketchPlane" : qUnion([Q0])});
            skLineSegment(sketch, "E208.bottom", {"start": v(-69, 51.8) * mm, "end": v(4, 51.8) * mm});
            skLineSegment(sketch, "E208.top", {"start": v(-69, -21.2) * mm, "end": v(4, -21.2) * mm});
            skLineSegment(sketch, "E208.left", {"start": v(-69, 51.8) * mm, "end": v(-69, -21.2) * mm});
            skLineSegment(sketch, "E208.right", {"start": v(4, 51.8) * mm, "end": v(4, -21.2) * mm});
            skLineSegment(sketch, "E209.bottom", {"start": v(8, -31.2) * mm, "end": v(-73, -31.2) * mm});
            skLineSegment(sketch, "E209.top", {"start": v(8, 55.8) * mm, "end": v(-73, 55.8) * mm});
            skLineSegment(sketch, "E209.left", {"start": v(8, -31.2) * mm, "end": v(8, 55.8) * mm});
            skLineSegment(sketch, "E209.right", {"start": v(-73, -31.2) * mm, "end": v(-73, 55.8) * mm});
            skCircle(sketch, "E210", {"center": v(-60.5, -26.2) * mm, "radius": 3 * mm});
            skCircle(sketch, "E211", {"center": v(-4.5, -26.2) * mm, "radius": 3 * mm});
            skLineSegment(sketch, "E212", {"start": v(-32.5, -31.2) * mm, "end": v(-32.5, -21.2) * mm, "construction": true});
            skLineSegment(sketch, "E213", {"start": v(-60.5, -26.2) * mm, "end": v(-32.5, -26.2) * mm, "construction": true});
            skLineSegment(sketch, "E214", {"start": v(-32.5, -26.2) * mm, "end": v(-4.5, -26.2) * mm, "construction": true});
            skSolve(sketch);
        }
        {
            var Q0;
            Q0 = qSketchRegion(id + "F19", true);
            extrude(context, id + "F20", {"entities" : qUnion([Q0]), "depth" : 4 * mm});
        }
        {
            var Q0;
            Q0=makeQuery(id+"F6.opExtrude","SWEPT_FACE",FACE,{"disambiguationData":[OSD([sQuery(id+"F5.wireOp",EDGE,"E92.right"),sQuery(id+"F5.wireOp",EDGE,"E93")])]});
            var sketch = newSketch(context, id + "F21", { "sketchPlane" : qUnion([Q0])});
            skPoint(sketch, "E215.visualSharp", {"position": v(-12.49, 26.88) * mm});
            skCircle(sketch, "E216", {"center": v(19.25, 23.09) * mm, "radius": 9.25 * mm});
            skArc(sketch, "E217", {"start": v(19.25, 38.34) * mm, "mid": v(8.47, 33.87) * mm, "end": v(4, 23.09) * mm});
            skArc(sketch, "E218", {"start": v(34.5, 23.09) * mm, "mid": v(30.03, 33.87) * mm, "end": v(19.25, 38.34) * mm});
            skLineSegment(sketch, "E219", {"start": v(34.5, 23.09) * mm, "end": v(197.5, 23.09) * mm});
            skLineSegment(sketch, "E220.bottom", {"start": v(36.68, 19.09) * mm, "end": v(57.67, 19.09) * mm});
            skLineSegment(sketch, "E220.top", {"start": v(34.5, -2.91) * mm, "end": v(55.49, -2.91) * mm});
            skLineSegment(sketch, "E220.left", {"start": v(34.5, 17.02) * mm, "end": v(34.5, -2.91) * mm});
            skLineSegment(sketch, "E220.right", {"start": v(57.67, 19.09) * mm, "end": v(57.67, -0.84) * mm});
            skLineSegment(sketch, "E221", {"start": v(34.5, 23.09) * mm, "end": v(34.5, 19.09) * mm, "construction": true});
            skLineSegment(sketch, "E222", {"start": v(34.5, -2.91) * mm, "end": v(34.5, -6.91) * mm, "construction": true});
            skLineSegment(sketch, "E223", {"start": v(34.5, 19.09) * mm, "end": v(57.67, -2.91) * mm, "construction": true});
            skLineSegment(sketch, "E224", {"start": v(36.68, 19.09) * mm, "end": v(57.67, -0.84) * mm});
            skLineSegment(sketch, "E225", {"start": v(55.49, -2.91) * mm, "end": v(34.5, 17.02) * mm});
            skLineSegment(sketch, "E226.1.0.0", {"start": v(82.65, -2.91) * mm, "end": v(61.67, 17.02) * mm});
            skLineSegment(sketch, "E226.1.0.1", {"start": v(84.83, 19.09) * mm, "end": v(84.83, -0.84) * mm});
            skLineSegment(sketch, "E226.1.0.2", {"start": v(61.67, 17.02) * mm, "end": v(61.67, -2.91) * mm});
            skLineSegment(sketch, "E226.1.0.3", {"start": v(61.67, -2.91) * mm, "end": v(61.67, -6.91) * mm, "construction": true});
            skLineSegment(sketch, "E226.1.0.4", {"start": v(61.67, 19.09) * mm, "end": v(84.83, -2.91) * mm, "construction": true});
            skLineSegment(sketch, "E226.1.0.5", {"start": v(63.84, 19.09) * mm, "end": v(84.83, 19.09) * mm});
            skLineSegment(sketch, "E226.1.0.6", {"start": v(61.67, -2.91) * mm, "end": v(82.65, -2.91) * mm});
            skLineSegment(sketch, "E226.1.0.7", {"start": v(63.84, 19.09) * mm, "end": v(84.83, -0.84) * mm});
            skLineSegment(sketch, "E226.1.0.8", {"start": v(61.67, 23.09) * mm, "end": v(61.67, 19.09) * mm, "construction": true});
            skLineSegment(sketch, "E226.2.0.0", {"start": v(109.82, -2.91) * mm, "end": v(88.83, 17.02) * mm});
            skLineSegment(sketch, "E226.2.0.1", {"start": v(112, 19.09) * mm, "end": v(112, -0.84) * mm});
            skLineSegment(sketch, "E226.2.0.2", {"start": v(88.83, 17.02) * mm, "end": v(88.83, -2.91) * mm});
            skLineSegment(sketch, "E226.2.0.3", {"start": v(88.83, -2.91) * mm, "end": v(88.83, -6.91) * mm, "construction": true});
            skLineSegment(sketch, "E226.2.0.4", {"start": v(88.83, 19.09) * mm, "end": v(112, -2.91) * mm, "construction": true});
            skLineSegment(sketch, "E226.2.0.5", {"start": v(91.01, 19.09) * mm, "end": v(112, 19.09) * mm});
            skLineSegment(sketch, "E226.2.0.6", {"start": v(88.83, -2.91) * mm, "end": v(109.82, -2.91) * mm});
            skLineSegment(sketch, "E226.2.0.7", {"start": v(91.01, 19.09) * mm, "end": v(112, -0.84) * mm});
            skLineSegment(sketch, "E226.2.0.8", {"start": v(88.83, 23.09) * mm, "end": v(88.83, 19.09) * mm, "construction": true});
            skLineSegment(sketch, "E226.3.0.0", {"start": v(136.99, -2.91) * mm, "end": v(116, 17.02) * mm});
            skLineSegment(sketch, "E226.3.0.1", {"start": v(139.17, 19.09) * mm, "end": v(139.17, -0.84) * mm});
            skLineSegment(sketch, "E226.3.0.2", {"start": v(116, 17.02) * mm, "end": v(116, -2.91) * mm});
            skLineSegment(sketch, "E226.3.0.3", {"start": v(116, -2.91) * mm, "end": v(116, -6.91) * mm, "construction": true});
            skLineSegment(sketch, "E226.3.0.4", {"start": v(116, 19.09) * mm, "end": v(139.17, -2.91) * mm, "construction": true});
            skLineSegment(sketch, "E226.3.0.5", {"start": v(118.18, 19.09) * mm, "end": v(139.17, 19.09) * mm});
            skLineSegment(sketch, "E226.3.0.6", {"start": v(116, -2.91) * mm, "end": v(136.99, -2.91) * mm});
            skLineSegment(sketch, "E226.3.0.7", {"start": v(118.18, 19.09) * mm, "end": v(139.17, -0.84) * mm});
            skLineSegment(sketch, "E226.3.0.8", {"start": v(116, 23.09) * mm, "end": v(116, 19.09) * mm, "construction": true});
            skLineSegment(sketch, "E226.4.0.0", {"start": v(164.15, -2.91) * mm, "end": v(143.17, 17.02) * mm});
            skLineSegment(sketch, "E226.4.0.1", {"start": v(166.33, 19.09) * mm, "end": v(166.33, -0.84) * mm});
            skLineSegment(sketch, "E226.4.0.2", {"start": v(143.17, 17.02) * mm, "end": v(143.17, -2.91) * mm});
            skLineSegment(sketch, "E226.4.0.3", {"start": v(143.17, -2.91) * mm, "end": v(143.17, -6.91) * mm, "construction": true});
            skLineSegment(sketch, "E226.4.0.4", {"start": v(143.17, 19.09) * mm, "end": v(166.33, -2.91) * mm, "construction": true});
            skLineSegment(sketch, "E226.4.0.5", {"start": v(145.34, 19.09) * mm, "end": v(166.33, 19.09) * mm});
            skLineSegment(sketch, "E226.4.0.6", {"start": v(143.17, -2.91) * mm, "end": v(164.15, -2.91) * mm});
            skLineSegment(sketch, "E226.4.0.7", {"start": v(145.34, 19.09) * mm, "end": v(166.33, -0.84) * mm});
            skLineSegment(sketch, "E226.4.0.8", {"start": v(143.17, 23.09) * mm, "end": v(143.17, 19.09) * mm, "construction": true});
            skLineSegment(sketch, "E226.5.0.0", {"start": v(191.32, -2.91) * mm, "end": v(170.33, 17.02) * mm});
            skLineSegment(sketch, "E226.5.0.1", {"start": v(193.5, 19.09) * mm, "end": v(193.5, -0.84) * mm});
            skLineSegment(sketch, "E226.5.0.2", {"start": v(170.33, 17.02) * mm, "end": v(170.33, -2.91) * mm});
            skLineSegment(sketch, "E226.5.0.3", {"start": v(170.33, -2.91) * mm, "end": v(170.33, -6.91) * mm, "construction": true});
            skLineSegment(sketch, "E226.5.0.4", {"start": v(170.33, 19.09) * mm, "end": v(193.5, -2.91) * mm, "construction": true});
            skLineSegment(sketch, "E226.5.0.5", {"start": v(172.51, 19.09) * mm, "end": v(193.5, 19.09) * mm});
            skLineSegment(sketch, "E226.5.0.6", {"start": v(170.33, -2.91) * mm, "end": v(191.32, -2.91) * mm});
            skLineSegment(sketch, "E226.5.0.7", {"start": v(172.51, 19.09) * mm, "end": v(193.5, -0.84) * mm});
            skLineSegment(sketch, "E226.5.0.8", {"start": v(170.33, 23.09) * mm, "end": v(170.33, 19.09) * mm, "construction": true});
            skLineSegment(sketch, "E226.direction1", {"start": v(34.5, 17.02) * mm, "end": v(61.67, 17.02) * mm, "construction": true});
            skLineSegment(sketch, "E227", {"start": v(197.5, 23.09) * mm, "end": v(197.5, -6.91) * mm});
            skLineSegment(sketch, "E228", {"start": v(197.5, -6.91) * mm, "end": v(-32.5, -6.91) * mm});
            skArc(sketch, "E229", {"start": v(-34.52, 0.54) * mm, "mid": v(-36.36, -3.96) * mm, "end": v(-32.5, -6.91) * mm});
            skLineSegment(sketch, "E230", {"start": v(4, 23.09) * mm, "end": v(-34.52, 0.54) * mm});
            skSolve(sketch);
        }
        {
            var Q0;
            Q0 = qSketchRegion(id + "F21", true);
            extrude(context, id + "F22", {"entities" : qUnion([Q0]), "depth" : 4 * mm});
        }
        {
            var Q0;
            Q0=makeQuery(id+"F2.opExtrude","CAP_FACE",FACE,{"disambiguationData":[OSD([sQuery(id+"F1.wireOp",EDGE,"E2"),sQuery(id+"F1.wireOp",EDGE,"E3"),sQuery(id+"F1.wireOp",EDGE,"E4"),sQuery(id+"F1.wireOp",EDGE,"E5"),sQuery(id+"F1.wireOp",EDGE,"E7"),sQuery(id+"F1.wireOp",EDGE,"E8"),sQuery(id+"F1.wireOp",EDGE,"E9"),sQuery(id+"F1.wireOp",EDGE,"E10"),sQuery(id+"F1.wireOp",EDGE,"E11"),sQuery(id+"F1.wireOp",EDGE,"E12"),sQuery(id+"F1.wireOp",EDGE,"E13"),sQuery(id+"F1.wireOp",EDGE,"E14"),sQuery(id+"F1.wireOp",EDGE,"E15"),sQuery(id+"F1.wireOp",EDGE,"E16"),sQuery(id+"F1.wireOp",EDGE,"E17"),sQuery(id+"F1.wireOp",EDGE,"E19.trimOffspring"),sQuery(id+"F1.wireOp",EDGE,"E20.trimOffspring"),sQuery(id+"F1.wireOp",EDGE,"E21.trimOffspring"),sQuery(id+"F1.wireOp",EDGE,"E22.trimOffspring"),sQuery(id+"F1.wireOp",EDGE,"E23.bottom"),sQuery(id+"F1.wireOp",EDGE,"E23.top"),sQuery(id+"F1.wireOp",EDGE,"E23.left"),sQuery(id+"F1.wireOp",EDGE,"E23.right"),sQuery(id+"F1.wireOp",EDGE,"E24.trimOffspring"),sQuery(id+"F1.wireOp",EDGE,"E25")])],"isStart":true});
            var sketch = newSketch(context, id + "F23", { "sketchPlane" : qUnion([Q0])});
            skLineSegment(sketch, "E231.0", {"start": v(-118.18, 19.09) * mm, "end": v(-139.17, -0.84) * mm});
            skLineSegment(sketch, "E232.0", {"start": v(-34.5, 23.09) * mm, "end": v(-197.5, 23.09) * mm});
            skLineSegment(sketch, "E233.0", {"start": v(-118.18, 19.09) * mm, "end": v(-139.17, 19.09) * mm});
            skLineSegment(sketch, "E234.0", {"start": v(-139.17, 19.09) * mm, "end": v(-139.17, -0.84) * mm});
            skLineSegment(sketch, "E235.0", {"start": v(-145.34, 19.09) * mm, "end": v(-166.33, -0.84) * mm});
            skLineSegment(sketch, "E236.0", {"start": v(-164.15, -2.91) * mm, "end": v(-143.17, 17.02) * mm});
            skLineSegment(sketch, "E237.0", {"start": v(-143.17, 17.02) * mm, "end": v(-143.17, -2.91) * mm});
            skLineSegment(sketch, "E238.0", {"start": v(-145.34, 19.09) * mm, "end": v(-166.33, 19.09) * mm});
            skLineSegment(sketch, "E239.0", {"start": v(-166.33, 19.09) * mm, "end": v(-166.33, -0.84) * mm});
            skLineSegment(sketch, "E240.0", {"start": v(-172.51, 19.09) * mm, "end": v(-193.5, -0.84) * mm});
            skLineSegment(sketch, "E241.0", {"start": v(-191.32, -2.91) * mm, "end": v(-170.33, 17.02) * mm});
            skLineSegment(sketch, "E242.0", {"start": v(-170.33, 17.02) * mm, "end": v(-170.33, -2.91) * mm});
            skLineSegment(sketch, "E243.0", {"start": v(-172.51, 19.09) * mm, "end": v(-193.5, 19.09) * mm});
            skLineSegment(sketch, "E244.0", {"start": v(-193.5, 19.09) * mm, "end": v(-193.5, -0.84) * mm});
            skLineSegment(sketch, "E245.0", {"start": v(-197.5, 23.09) * mm, "end": v(-197.5, -6.91) * mm});
            skLineSegment(sketch, "E246.0", {"start": v(-197.5, -6.91) * mm, "end": v(-4, -6.91) * mm});
            skLineSegment(sketch, "E247.0", {"start": v(-143.17, -2.91) * mm, "end": v(-164.15, -2.91) * mm});
            skLineSegment(sketch, "E248.0", {"start": v(-136.99, -2.91) * mm, "end": v(-116, 17.02) * mm});
            skLineSegment(sketch, "E249.0", {"start": v(-116, -2.91) * mm, "end": v(-136.99, -2.91) * mm});
            skLineSegment(sketch, "E250.0", {"start": v(-116, 17.02) * mm, "end": v(-116, -2.91) * mm});
            skLineSegment(sketch, "E251.0", {"start": v(-91.01, 19.09) * mm, "end": v(-112, -0.84) * mm});
            skLineSegment(sketch, "E252.0", {"start": v(-91.01, 19.09) * mm, "end": v(-112, 19.09) * mm});
            skLineSegment(sketch, "E253.0", {"start": v(-88.83, 17.02) * mm, "end": v(-88.83, -2.91) * mm});
            skLineSegment(sketch, "E254.0", {"start": v(-109.82, -2.91) * mm, "end": v(-88.83, 17.02) * mm});
            skLineSegment(sketch, "E255.0", {"start": v(-88.83, -2.91) * mm, "end": v(-109.82, -2.91) * mm});
            skLineSegment(sketch, "E256.0", {"start": v(-63.84, 19.09) * mm, "end": v(-84.83, -0.84) * mm});
            skLineSegment(sketch, "E257.0", {"start": v(-63.84, 19.09) * mm, "end": v(-84.83, 19.09) * mm});
            skLineSegment(sketch, "E258.0", {"start": v(-84.83, 19.09) * mm, "end": v(-84.83, -0.84) * mm});
            skLineSegment(sketch, "E259.0", {"start": v(-82.65, -2.91) * mm, "end": v(-61.67, 17.02) * mm});
            skLineSegment(sketch, "E260.0", {"start": v(-61.67, 17.02) * mm, "end": v(-61.67, -2.91) * mm});
            skLineSegment(sketch, "E261.0", {"start": v(-61.67, -2.91) * mm, "end": v(-82.65, -2.91) * mm});
            skLineSegment(sketch, "E262.0", {"start": v(-57.67, 19.09) * mm, "end": v(-57.67, -0.84) * mm});
            skLineSegment(sketch, "E263.0", {"start": v(-36.68, 19.09) * mm, "end": v(-57.67, -0.84) * mm});
            skLineSegment(sketch, "E264.0", {"start": v(-55.49, -2.91) * mm, "end": v(-34.5, 17.02) * mm});
            skLineSegment(sketch, "E265.0", {"start": v(-36.68, 19.09) * mm, "end": v(-57.67, 19.09) * mm});
            skLineSegment(sketch, "E266.0", {"start": v(-34.5, -2.91) * mm, "end": v(-55.49, -2.91) * mm});
            skLineSegment(sketch, "E267.0", {"start": v(-34.5, 17.02) * mm, "end": v(-34.5, -2.91) * mm});
            skCircle(sketch, "E268.0", {"center": v(-19.25, 23.09) * mm, "radius": 9.25 * mm});
            skArc(sketch, "E269.0", {"start": v(-34.5, 23.09) * mm, "mid": v(-19.25, 38.34) * mm, "end": v(-4, 23.09) * mm});
            skLineSegment(sketch, "E270", {"start": v(-4, 23.09) * mm, "end": v(-4, -6.91) * mm});
            skPoint(sketch, "E271.orphan", {"position": v(32.5, -6.91) * mm});
            skLineSegment(sketch, "E272", {"start": v(-170.33, -2.91) * mm, "end": v(-191.32, -2.91) * mm});
            skLineSegment(sketch, "E273", {"start": v(-112, -0.84) * mm, "end": v(-112, 19.09) * mm});
            skSolve(sketch);
        }
        {
            var Q0;
            Q0 = qSketchRegion(id + "F23", true);
            extrude(context, id + "F24", {"entities" : qUnion([Q0]), "depth" : 4 * mm});
        }
        {
            var Q0;
            Q0=makeQuery(id+"F24.opExtrude","SWEPT_FACE",FACE,{"disambiguationData":[OSD([sQuery(id+"F23.wireOp",EDGE,"E246.0")])]});
            var sketch = newSketch(context, id + "F25", { "sketchPlane" : qUnion([Q0])});
            skLineSegment(sketch, "E274.bottom", {"start": v(197.5, 0) * mm, "end": v(72.5, 0) * mm});
            skLineSegment(sketch, "E274.top", {"start": v(197.5, -76) * mm, "end": v(72.5, -76) * mm});
            skLineSegment(sketch, "E274.left", {"start": v(197.5, 0) * mm, "end": v(197.5, -76) * mm});
            skLineSegment(sketch, "E274.right", {"start": v(72.5, 0) * mm, "end": v(72.5, -76) * mm});
            skSolve(sketch);
        }
        {
            var Q0;
            Q0 = qSketchRegion(id + "F25", true);
            extrude(context, id + "F26", {"entities" : qUnion([Q0]), "depth" : 4 * mm});
        }
        {
            var Q0;
            Q0=makeQuery(id+"F6.opExtrude","SWEPT_FACE",FACE,{"disambiguationData":[OSD([sQuery(id+"F5.wireOp",EDGE,"E111.left")])]});
            var sketch = newSketch(context, id + "F27", { "sketchPlane" : qUnion([Q0])});
            skLineSegment(sketch, "E275", {"start": v(-4, 40.6) * mm, "end": v(0, 40.6) * mm});
            skLineSegment(sketch, "E276", {"start": v(0, 40.6) * mm, "end": v(0, 20.6) * mm});
            skLineSegment(sketch, "E277", {"start": v(0, 20.6) * mm, "end": v(-4, 20.6) * mm});
            skLineSegment(sketch, "E278", {"start": v(-4, 20.6) * mm, "end": v(-4, 12.6) * mm});
            skLineSegment(sketch, "E279", {"start": v(-4, 12.6) * mm, "end": v(0, 12.6) * mm});
            skLineSegment(sketch, "E280", {"start": v(0, 12.6) * mm, "end": v(0, -7.4) * mm});
            skLineSegment(sketch, "E281", {"start": v(0, -7.4) * mm, "end": v(-4, -7.4) * mm});
            skLineSegment(sketch, "E282", {"start": v(-4, -7.4) * mm, "end": v(-4, -17.3) * mm});
            skLineSegment(sketch, "E283", {"start": v(-4, -17.3) * mm, "end": v(-24, -17.3) * mm});
            skLineSegment(sketch, "E284", {"start": v(-39, -2.3) * mm, "end": v(-39, 33.07) * mm});
            skLineSegment(sketch, "E285", {"start": v(-24, 48.07) * mm, "end": v(-4, 48.07) * mm});
            skLineSegment(sketch, "E286", {"start": v(-4, 48.07) * mm, "end": v(-4, 40.6) * mm});
            skPoint(sketch, "E287.visualSharp", {"position": v(-39, 48.07) * mm});
            skArc(sketch, "E287.filletArc", {"start": v(-24, 48.07) * mm, "mid": v(-34.6, 43.67) * mm, "end": v(-39, 33.07) * mm});
            skPoint(sketch, "E288.visualSharp", {"position": v(-39, -17.3) * mm});
            skArc(sketch, "E288.filletArc", {"start": v(-39, -2.3) * mm, "mid": v(-34.6, -12.9) * mm, "end": v(-24, -17.3) * mm});
            skCircle(sketch, "E289", {"center": v(-19.25, 23.09) * mm, "radius": 2.5 * mm});
            skSolve(sketch);
        }
        {
            var Q0;
            Q0 = qSketchRegion(id + "F27", true);
            extrude(context, id + "F28", {"entities" : qUnion([Q0]), "depth" : 4 * mm});
        }
    });
